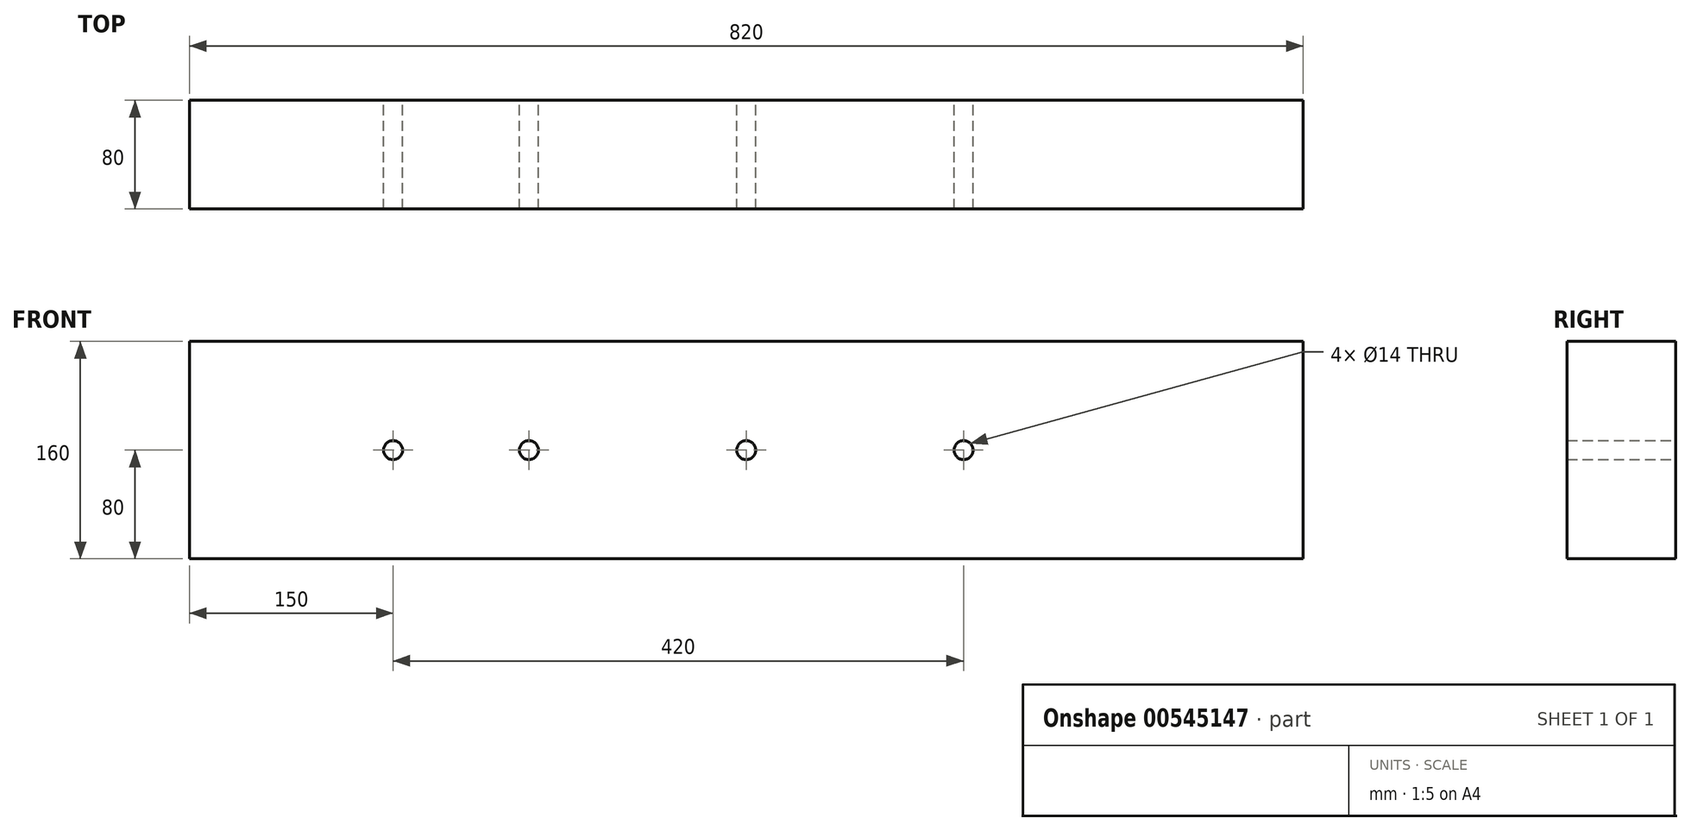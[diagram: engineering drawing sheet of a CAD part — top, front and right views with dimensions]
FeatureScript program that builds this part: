
annotation { "Feature Type Name" : "Feature", "Feature Type Description" : "" }
export const myFeature = defineFeature(function(context is Context, id is Id, definition is map)
    precondition{}
    {
        {
            var Q0;
            Q0=qCreatedBy(makeId("Front.planeOp"),FACE);
            var sketch = newSketch(context, id + "F0", { "sketchPlane" : qUnion([Q0])});
            skLineSegment(sketch, "E0.bottom", {"start": v(-410, 80) * mm, "end": v(410, 80) * mm});
            skLineSegment(sketch, "E0.top", {"start": v(-410, -80) * mm, "end": v(410, -80) * mm});
            skLineSegment(sketch, "E0.left", {"start": v(-410, 80) * mm, "end": v(-410, -80) * mm});
            skLineSegment(sketch, "E0.right", {"start": v(410, 80) * mm, "end": v(410, -80) * mm});
            skPoint(sketch, "E0.middle", {"position": v(0, 0) * mm});
            skCircle(sketch, "E1", {"center": v(0, 0) * mm, "radius": 7 * mm});
            skCircle(sketch, "E2", {"center": v(-160, 0) * mm, "radius": 7 * mm});
            skCircle(sketch, "E3", {"center": v(160, 0) * mm, "radius": 7 * mm});
            skCircle(sketch, "E4", {"center": v(-260, 0) * mm, "radius": 7 * mm});
            skSolve(sketch);
        }
        {
            var Q0;
            Q0=makeQuery(id+"F0.imprint","IMPRINT",FACE,{"disambiguationData":[TD([[makeQuery(id+"F0.imprint","IMPRINT",EDGE,{"derivedFrom":sQuery(id+"F0.wireOp",EDGE,"E0.bottom")}),-1.0]])]});
            extrude(context, id + "F1", {"entities" : qUnion([Q0]), "depth" : 80 * mm, "offsetDistance" : 25 * mm});
        }
    });
